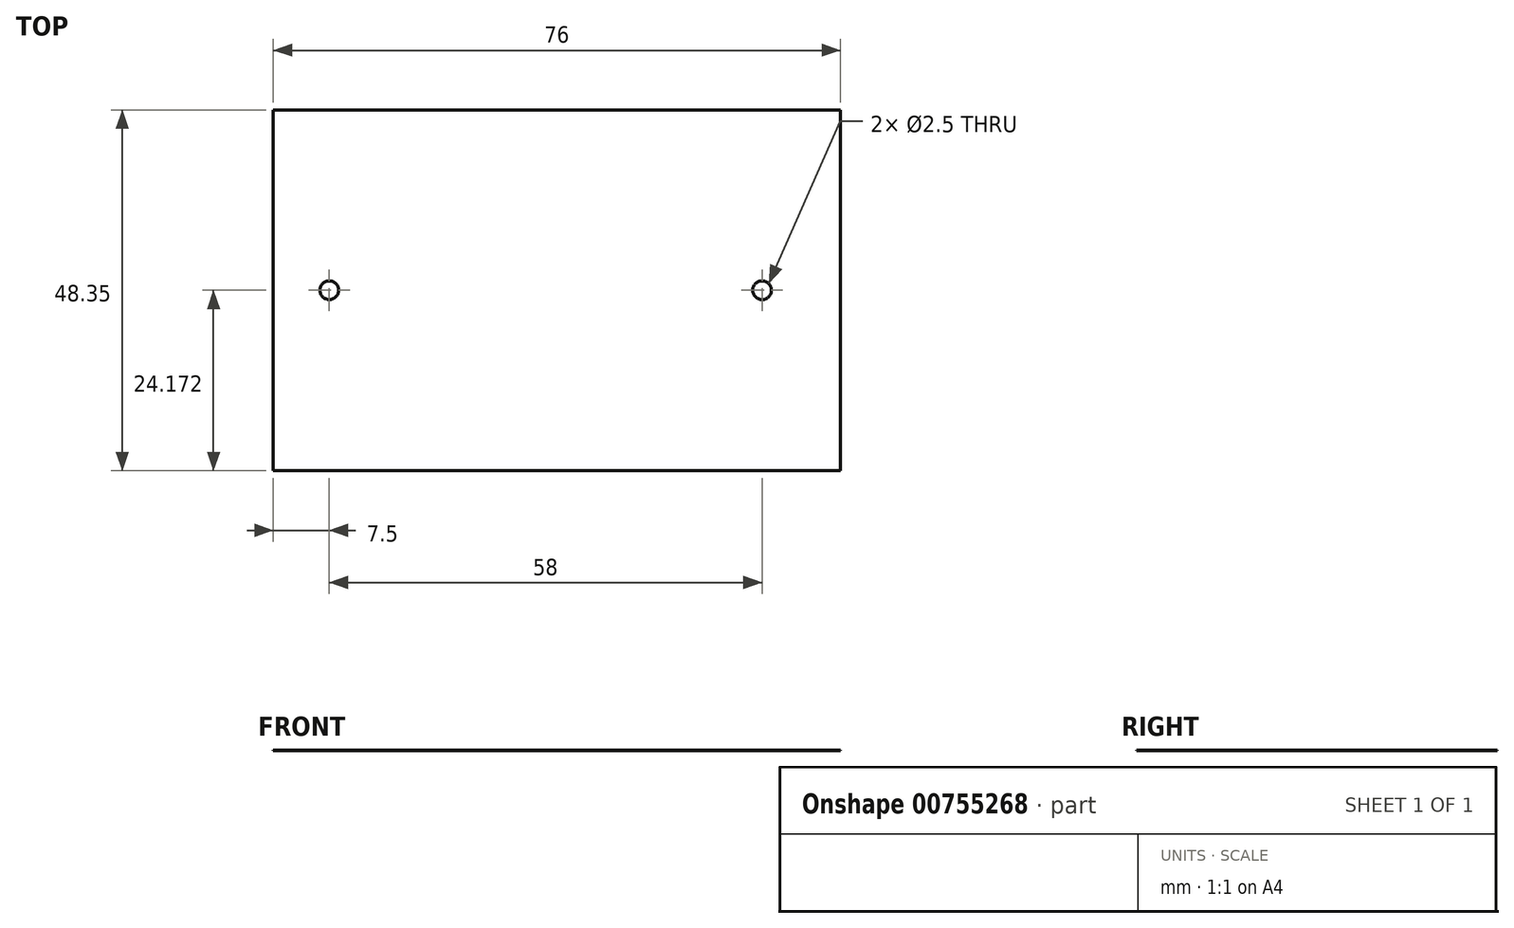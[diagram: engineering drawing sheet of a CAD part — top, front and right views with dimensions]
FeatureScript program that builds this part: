
annotation { "Feature Type Name" : "Feature", "Feature Type Description" : "" }
export const myFeature = defineFeature(function(context is Context, id is Id, definition is map)
    precondition{}
    {
        {
            var Q0;
            Q0=qCreatedBy(makeId("Top.planeOp"),FACE);
            var sketch = newSketch(context, id + "F0", { "sketchPlane" : qUnion([Q0])});
            skLineSegment(sketch, "E0", {"start": v(-17.56, 18.89) * mm, "end": v(58.44, 18.89) * mm});
            skLineSegment(sketch, "E1", {"start": v(58.44, 18.89) * mm, "end": v(58.44, -29.46) * mm});
            skLineSegment(sketch, "E2", {"start": v(58.44, -29.46) * mm, "end": v(-17.56, -29.46) * mm});
            skLineSegment(sketch, "E3", {"start": v(-17.56, 18.89) * mm, "end": v(-17.56, -29.46) * mm});
            skCircle(sketch, "E4", {"center": v(-10.06, -5.29) * mm, "radius": 1.25 * mm});
            skPoint(sketch, "E4.centerSnap0", {"position": v(28.34, -5.29) * mm});
            skCircle(sketch, "E5", {"center": v(47.94, -5.29) * mm, "radius": 1.25 * mm});
            skSolve(sketch);
        }
        {
            var Q0;
            {var subQ6=sQuery(id+"F0.wireOp",EDGE,"SYacwyzY-BZFg-imQt-Ttsi-c93llfWGmcYO.top");Q0=makeQuery(id+"F0.imprint","IMPRINT",FACE,{"disambiguationData":[TD([[makeQuery(id+"F0.imprint","IMPRINT",EDGE,{"derivedFrom":subQ6}),-1.0]])]});}
            var Q1;
            {var subQ4=sQuery(id+"F0.wireOp",EDGE,"P5kO2gDR-HQxe-fJ9V-a2Dj-CVA5tXInye47");Q1=makeQuery(id+"F0.imprint","IMPRINT",FACE,{"disambiguationData":[TD([[makeQuery(id+"F0.imprint","IMPRINT",EDGE,{"derivedFrom":subQ4}),-1.0]])]});}
            var Q2;
            {var subQ2=sQuery(id+"F0.wireOp",EDGE,"SYacwyzY-BZFg-imQt-Ttsi-c93llfWGmcYO.top");Q2=makeQuery(id+"F0.imprint","IMPRINT",FACE,{"disambiguationData":[TD([[makeQuery(id+"F0.imprint","IMPRINT",EDGE,{"derivedFrom":subQ2}),1.0]])]});}
            var Q3;
            {var subQ3=sQuery(id+"F0.wireOp",EDGE,"32cNfb66-weMd-p5yn-bAME-1WnTSvuJrZvc.bottom");Q3=makeQuery(id+"F0.imprint","IMPRINT",FACE,{"disambiguationData":[TD([[makeQuery(id+"F0.imprint","IMPRINT",EDGE,{"derivedFrom":subQ3}),-1.0]])]});}
            var Q4;
            Q4=makeQuery(id+"F0.imprint","IMPRINT",FACE,{"disambiguationData":[TD([[makeQuery(id+"F0.imprint","IMPRINT",EDGE,{"derivedFrom":sQuery(id+"F0.wireOp",EDGE,"E0")}),-1.0]])]});
            extrude(context, id + "F1", {"entities" : qUnion([Q0, Q1, Q2, Q3, Q4]), "depth" : 1 / 203.2 * mm, "offsetDistance" : 25 * mm});
        }
    });
